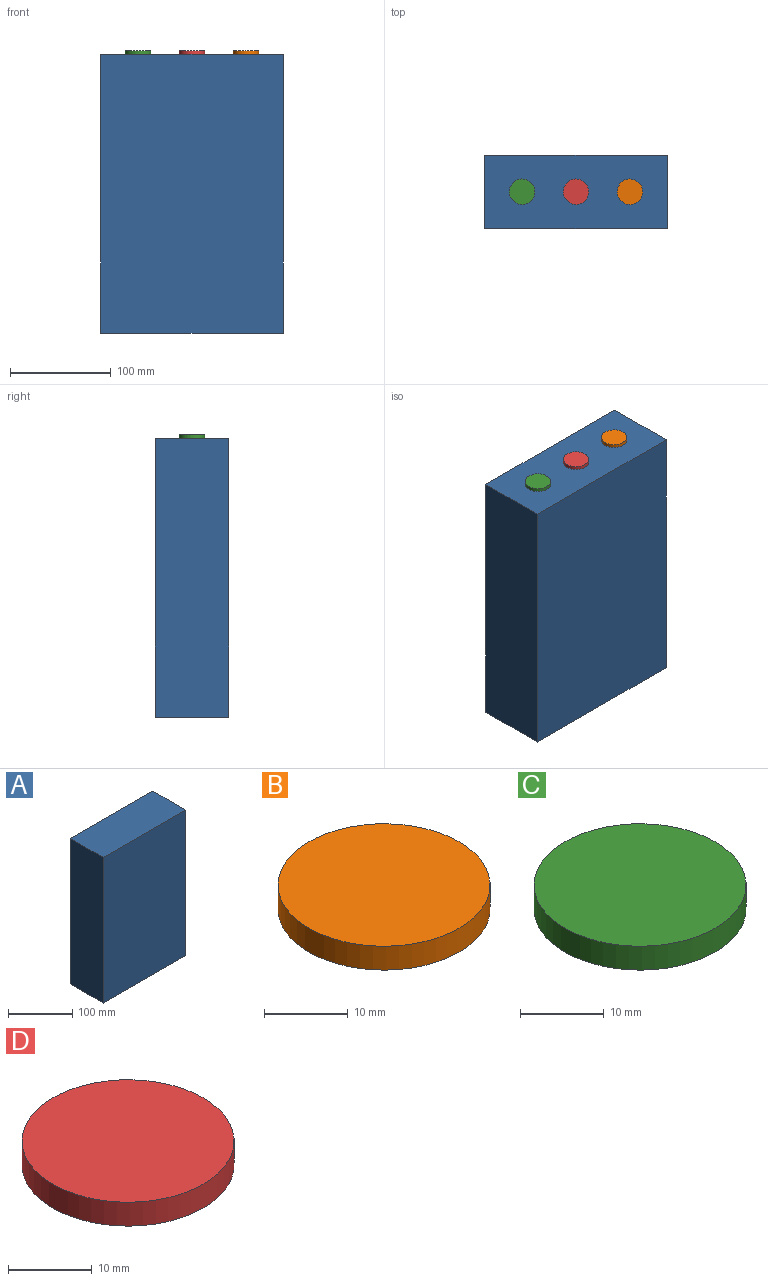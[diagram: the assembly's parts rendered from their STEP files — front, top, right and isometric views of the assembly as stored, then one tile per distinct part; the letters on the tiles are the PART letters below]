
ASSEMBLY  parts=4 mates=3
PART A: 6 faces, bbox 181x72.5x277 mm
  f0: plane 277x72.5mm, normal (-1,0,0), area 20082.5mm2, adj f1,f3,f4,f5
  f1: plane 277x181mm, normal (0,-1,0), area 50137mm2, adj f0,f2,f4,f5
  f2: plane 277x72.5mm, normal (1,0,0), area 20082.5mm2, adj f1,f3,f4,f5
  f3: plane 277x181mm, normal (0,1,0), area 50137mm2, adj f0,f2,f4,f5
  f4: plane 181x72.5mm, normal (0,0,1), area 13122.5mm2, adj f0,f1,f2,f3
  f5: plane 181x72.5mm, normal (0,0,-1), area 13122.5mm2, adj f0,f1,f2,f3
PART B: 3 faces, bbox 25.4x25.4x3.5 mm
  f0: cylinder r=12.7mm len=25.4mm, axis (0,0,-1), area 279.3mm2, adj f1,f2
  f1: plane 25.4x25.4mm, normal (0,0,1), area 506.7mm2, adj f0
  f2: plane 25.4x25.4mm, normal (0,0,-1), area 506.7mm2, adj f0
PART C: 3 faces, bbox 25.4x25.4x3.5 mm
  f0: cylinder r=12.7mm len=25.4mm, axis (0,0,-1), area 279.3mm2, adj f1,f2
  f1: plane 25.4x25.4mm, normal (0,0,1), area 506.7mm2, adj f0
  f2: plane 25.4x25.4mm, normal (0,0,-1), area 506.7mm2, adj f0
PART D: 3 faces, bbox 25.4x25.4x3.5 mm
  f0: cylinder r=12.7mm len=25.4mm, axis (0,0,-1), area 279.3mm2, adj f1,f2
  f1: plane 25.4x25.4mm, normal (0,0,1), area 506.7mm2, adj f0
  f2: plane 25.4x25.4mm, normal (0,0,-1), area 506.7mm2, adj f0
PLACE A t=(-90.5,0,0)mm
PLACE B t=(-90,0,0)mm
PLACE C t=(-91,0,0)mm
PLACE D t=(-90.5,0,0)mm
MATE fastened C.f0 <-> A.f4  axis (0,0,-1) through (-144,36.25,277)mm
MATE fastened D.f0 <-> A.f4  axis (0,0,-1) through (-90.5,36.25,277)mm
MATE fastened B.f0 <-> A.f4  axis (0,0,-1) through (-37,36.25,277)mm
